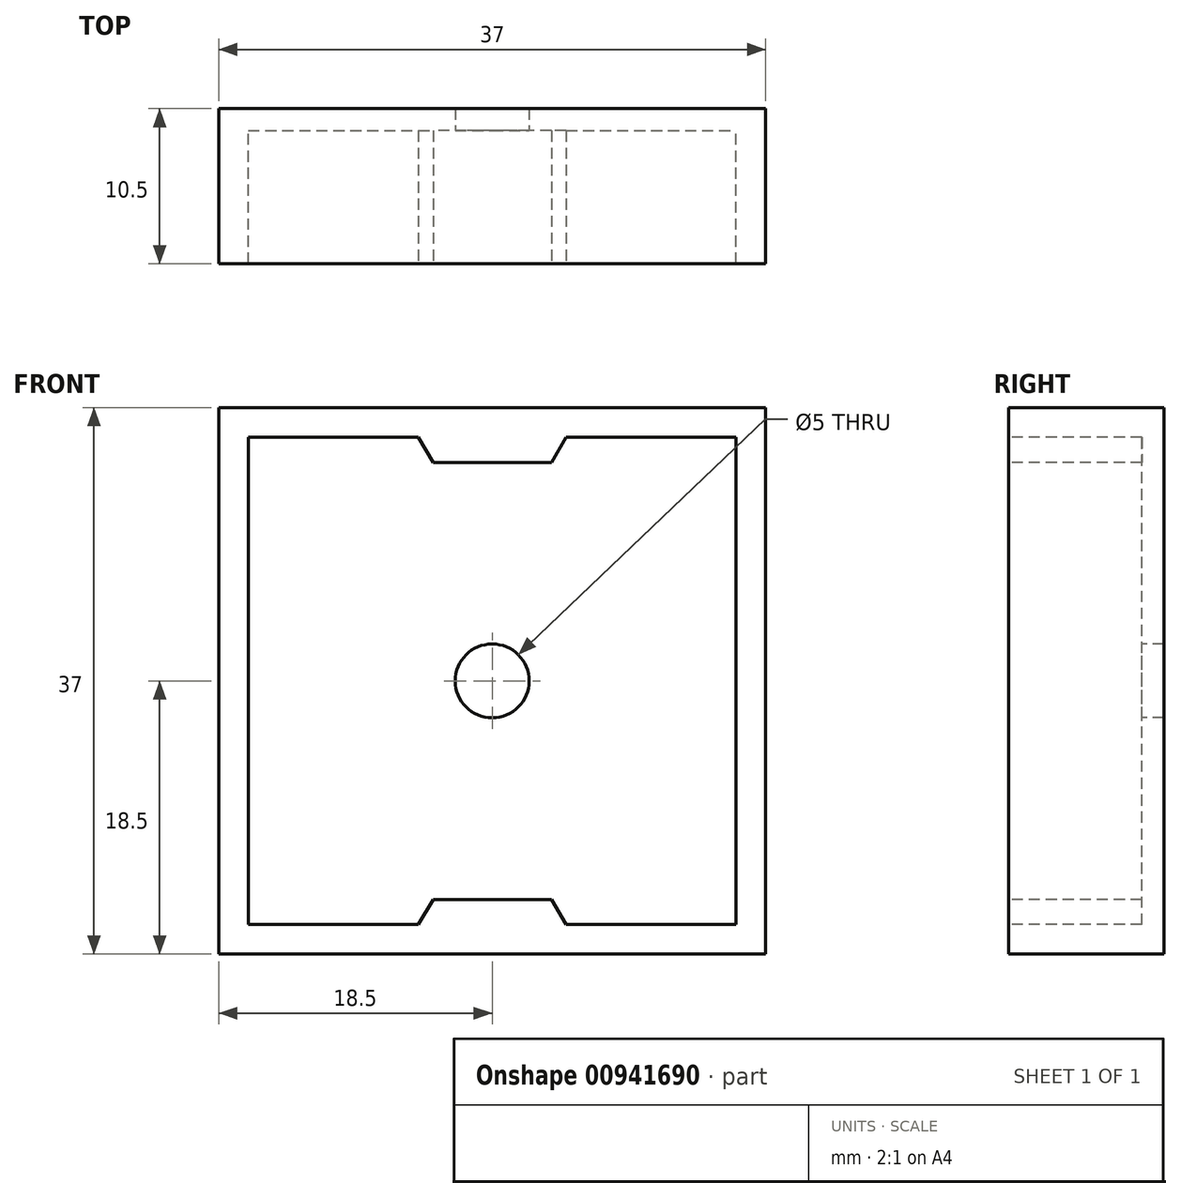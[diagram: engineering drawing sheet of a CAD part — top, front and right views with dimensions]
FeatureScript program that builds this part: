
annotation { "Feature Type Name" : "Feature", "Feature Type Description" : "" }
export const myFeature = defineFeature(function(context is Context, id is Id, definition is map)
    precondition{}
    {
        {
            var Q0;
            Q0=qCreatedBy(makeId("Front.planeOp"),FACE);
            var sketch = newSketch(context, id + "F0", { "sketchPlane" : qUnion([Q0])});
            skLineSegment(sketch, "E0.bottom", {"start": v(0, 0) * mm, "end": v(37, 0) * mm});
            skLineSegment(sketch, "E0.top", {"start": v(0, 37) * mm, "end": v(37, 37) * mm});
            skLineSegment(sketch, "E0.left", {"start": v(0, 0) * mm, "end": v(0, 37) * mm});
            skLineSegment(sketch, "E0.right", {"start": v(37, 0) * mm, "end": v(37, 37) * mm});
            skLineSegment(sketch, "E1.0", {"start": v(2, 2) * mm, "end": v(35, 2) * mm});
            skLineSegment(sketch, "E1.1", {"start": v(2, 2) * mm, "end": v(2, 35) * mm});
            skLineSegment(sketch, "E1.2", {"start": v(2, 35) * mm, "end": v(35, 35) * mm});
            skLineSegment(sketch, "E1.3", {"start": v(35, 2) * mm, "end": v(35, 35) * mm});
            skSolve(sketch);
        }
        {
            var Q0;
            Q0 = qSketchRegion(id + "F0", true);
            extrude(context, id + "F1", {"entities" : qUnion([Q0]), "depth" : 9 * mm, "offsetDistance" : 25 * mm});
        }
        {
            var Q0;
            Q0=makeQuery(id+"F1.opExtrude","CAP_FACE",FACE,{"disambiguationData":[OSD([sQuery(id+"F0.wireOp",EDGE,"E0.bottom"),sQuery(id+"F0.wireOp",EDGE,"E0.top"),sQuery(id+"F0.wireOp",EDGE,"E0.left"),sQuery(id+"F0.wireOp",EDGE,"E0.right"),sQuery(id+"F0.wireOp",EDGE,"E1.0"),sQuery(id+"F0.wireOp",EDGE,"E1.1"),sQuery(id+"F0.wireOp",EDGE,"E1.2"),sQuery(id+"F0.wireOp",EDGE,"E1.3")])],"isStart":true});
            var sketch = newSketch(context, id + "F2", { "sketchPlane" : qUnion([Q0])});
            skLineSegment(sketch, "E2.bottom", {"start": v(0, 0) * mm, "end": v(-37, 0) * mm});
            skLineSegment(sketch, "E2.top", {"start": v(0, 37) * mm, "end": v(-37, 37) * mm});
            skLineSegment(sketch, "E2.left", {"start": v(0, 0) * mm, "end": v(0, 37) * mm});
            skLineSegment(sketch, "E2.right", {"start": v(-37, 0) * mm, "end": v(-37, 37) * mm});
            skSolve(sketch);
        }
        {
            var Q0;
            Q0 = qSketchRegion(id + "F2", true);
            extrude(context, id + "F3", {"entities" : qUnion([Q0]), "operationType" : NewBodyOperationType.ADD, "depth" : 1.5 * mm, "offsetDistance" : 25 * mm});
        }
        {
            var Q0;
            Q0=makeQuery(id+"F1.opExtrude","CAP_FACE",FACE,{"disambiguationData":[OSD([sQuery(id+"F0.wireOp",EDGE,"E0.bottom"),sQuery(id+"F0.wireOp",EDGE,"E0.top"),sQuery(id+"F0.wireOp",EDGE,"E0.left"),sQuery(id+"F0.wireOp",EDGE,"E0.right"),sQuery(id+"F0.wireOp",EDGE,"E1.0"),sQuery(id+"F0.wireOp",EDGE,"E1.1"),sQuery(id+"F0.wireOp",EDGE,"E1.2"),sQuery(id+"F0.wireOp",EDGE,"E1.3")])],"isStart":false});
            var sketch = newSketch(context, id + "F4", { "sketchPlane" : qUnion([Q0])});
            skLineSegment(sketch, "E3", {"start": v(13.5, 35) * mm, "end": v(14.5, 33.3) * mm});
            skLineSegment(sketch, "E4", {"start": v(18.5, 35) * mm, "end": v(18.5, 29.43) * mm, "construction": true});
            skLineSegment(sketch, "E5.MirrorCS", {"start": v(23.5, 35) * mm, "end": v(22.5, 33.3) * mm});
            skLineSegment(sketch, "E6", {"start": v(2, 18.5) * mm, "end": v(8.97, 18.5) * mm, "construction": true});
            skLineSegment(sketch, "E7", {"start": v(13.5, 35) * mm, "end": v(23.5, 35) * mm});
            skLineSegment(sketch, "E8", {"start": v(22.5, 33.3) * mm, "end": v(14.5, 33.3) * mm});
            skLineSegment(sketch, "E9.MirrorCS", {"start": v(13.5, 2) * mm, "end": v(14.5, 3.7) * mm});
            skLineSegment(sketch, "E10.MirrorCS", {"start": v(13.5, 2) * mm, "end": v(23.5, 2) * mm});
            skLineSegment(sketch, "E11.MirrorCS", {"start": v(22.5, 3.7) * mm, "end": v(14.5, 3.7) * mm});
            skLineSegment(sketch, "E12.MirrorCS", {"start": v(23.5, 2) * mm, "end": v(22.5, 3.7) * mm});
            skSolve(sketch);
        }
        {
            var Q0;
            Q0 = qSketchRegion(id + "F4", true);
            var Q1;
            Q1=makeQuery(id+"F3.opExtrude","CAP_FACE",FACE,{"disambiguationData":[OSD([sQuery(id+"F2.wireOp",EDGE,"E2.bottom"),sQuery(id+"F2.wireOp",EDGE,"E2.top"),sQuery(id+"F2.wireOp",EDGE,"E2.left"),sQuery(id+"F2.wireOp",EDGE,"E2.right")])],"isStart":true});
            extrude(context, id + "F5", {"entities" : qUnion([Q0]), "operationType" : NewBodyOperationType.ADD, "endBound" : BoundingType.UP_TO_SURFACE, "oppositeDirection" : true, "depth" : 25 * mm, "endBoundEntityFace" : qUnion([Q1]), "offsetDistance" : 25 * mm});
        }
        {
            var Q0;
            Q0=makeQuery(id+"F3.opExtrude","CAP_FACE",FACE,{"disambiguationData":[OSD([sQuery(id+"F2.wireOp",EDGE,"E2.bottom"),sQuery(id+"F2.wireOp",EDGE,"E2.top"),sQuery(id+"F2.wireOp",EDGE,"E2.left"),sQuery(id+"F2.wireOp",EDGE,"E2.right")])],"isStart":true});
            var sketch = newSketch(context, id + "F6", { "sketchPlane" : qUnion([Q0])});
            skPoint(sketch, "E13", {"position": v(18.5, 18.5) * mm});
            skLineSegment(sketch, "E14", {"start": v(18.5, 18.5) * mm, "end": v(18.5, 33.3) * mm, "construction": true});
            skLineSegment(sketch, "E15", {"start": v(18.5, 18.5) * mm, "end": v(2, 18.5) * mm, "construction": true});
            skSolve(sketch);
        }
        {
            var Q0;
            Q0=sQuery(id+"F6.wireOp",VERTEX,"E13");
            var Q1;
            Q1=makeQuery(id+"F1.opExtrude","SWEPT_BODY",BODY,{"disambiguationData":[OSD([sQuery(id+"F0.wireOp",EDGE,"E0.bottom"),sQuery(id+"F0.wireOp",EDGE,"E0.top"),sQuery(id+"F0.wireOp",EDGE,"E0.left"),sQuery(id+"F0.wireOp",EDGE,"E0.right"),sQuery(id+"F0.wireOp",EDGE,"E1.0"),sQuery(id+"F0.wireOp",EDGE,"E1.1"),sQuery(id+"F0.wireOp",EDGE,"E1.2"),sQuery(id+"F0.wireOp",EDGE,"E1.3")])]});
            hole(context, id + "F7", {"style" : HoleStyle.SIMPLE, "endStyle" : HoleEndStyle.THROUGH, "holeDiameter" : 5 * mm, "majorDiameter" : 5 * mm, "isTappedThrough" : true, "tappedDepth" : 12 * mm, "tapClearance" : 3, "locations" : qUnion([Q0]), "scope" : qUnion([Q1])});
        }
    });
